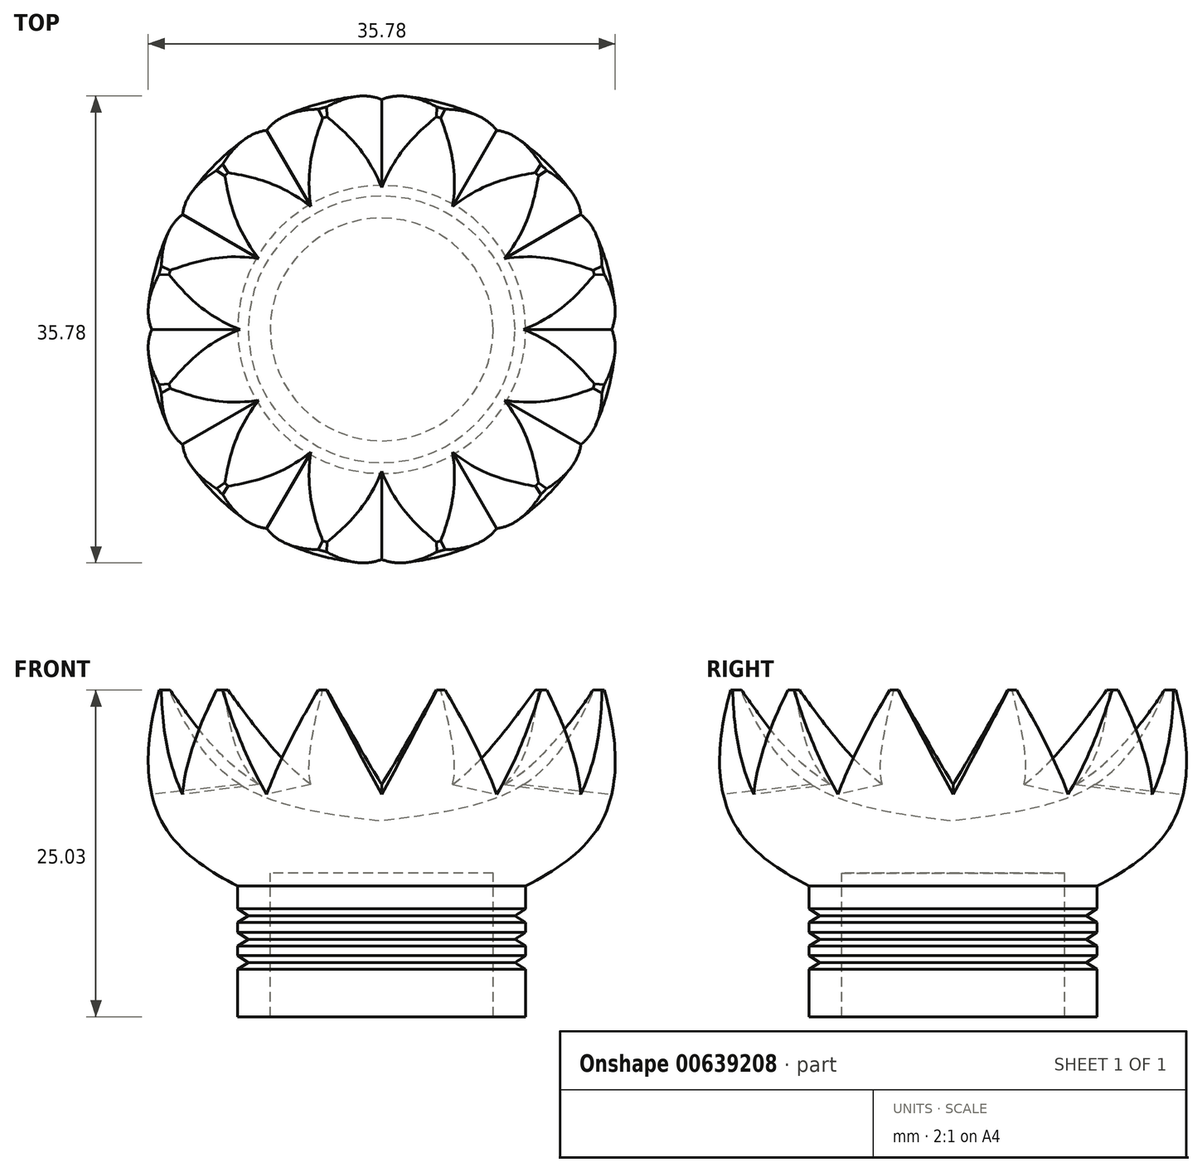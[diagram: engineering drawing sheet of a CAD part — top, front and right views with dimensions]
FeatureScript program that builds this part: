
annotation { "Feature Type Name" : "Feature", "Feature Type Description" : "" }
export const myFeature = defineFeature(function(context is Context, id is Id, definition is map)
    precondition{}
    {
        {
            var Q0;
            Q0=qCreatedBy(makeId("Front.planeOp"),FACE);
            var sketch = newSketch(context, id + "F0", { "sketchPlane" : qUnion([Q0])});
            skLineSegment(sketch, "E0", {"start": v(0, 11) * mm, "end": v(-8.54, 11) * mm});
            skLineSegment(sketch, "E1", {"start": v(-8.54, 11) * mm, "end": v(-8.54, 0) * mm});
            skLineSegment(sketch, "E2", {"start": v(-8.54, 0) * mm, "end": v(-11.04, 0) * mm});
            skLineSegment(sketch, "E3", {"start": v(-11.04, 0) * mm, "end": v(-11.04, 3.63) * mm});
            skLineSegment(sketch, "E4", {"start": v(-11.04, 3.63) * mm, "end": v(-10.22, 4.14) * mm});
            skLineSegment(sketch, "E5", {"start": v(-10.22, 4.14) * mm, "end": v(-11.04, 4.68) * mm});
            skLineSegment(sketch, "E6", {"start": v(-11.04, 4.68) * mm, "end": v(-11.04, 5.42) * mm});
            skLineSegment(sketch, "E7", {"start": v(-11.04, 5.42) * mm, "end": v(-10.22, 5.94) * mm});
            skLineSegment(sketch, "E8", {"start": v(-10.22, 5.94) * mm, "end": v(-11.04, 6.47) * mm});
            skLineSegment(sketch, "E9", {"start": v(-11.04, 6.47) * mm, "end": v(-11.04, 7.21) * mm});
            skLineSegment(sketch, "E10", {"start": v(-11.04, 7.21) * mm, "end": v(-10.22, 7.73) * mm});
            skLineSegment(sketch, "E11", {"start": v(-10.22, 7.73) * mm, "end": v(-11.04, 8.27) * mm});
            skLineSegment(sketch, "E12", {"start": v(-11.04, 8.27) * mm, "end": v(-11.04, 9) * mm});
            skLineSegment(sketch, "E13", {"start": v(-11.04, 9) * mm, "end": v(-11.04, 10.01) * mm});
            skFitSpline(sketch, "E14", {"points": [v(-11.04, 10.01) * mm, v(-16.97, 15.17) * mm, v(-17.56, 25.03) * mm], "startDerivative": vector(-16.56, 8.68) * mm, "endDerivative": vector(3.17, 21.15) * mm});
            skLineSegment(sketch, "E15", {"start": v(-17.56, 25.03) * mm, "end": v(-16.82, 25.03) * mm});
            skFitSpline(sketch, "E16", {"points": [v(-16.82, 25.03) * mm, v(-10.92, 17.83) * mm, v(0, 15.01) * mm], "startDerivative": vector(10.38, -17.46) * mm, "endDerivative": vector(23.06, -2.82) * mm});
            skLineSegment(sketch, "E17", {"start": v(0, 15.01) * mm, "end": v(0, 11) * mm});
            skSolve(sketch);
        }
        {
            var Q0;
            Q0 = qSketchRegion(id + "F0", true);
            var Q1;
            Q1=sQuery(id+"F0.wireOp",EDGE,"E17");
            revolve(context, id + "F1", {"entities" : qUnion([Q0]), "axis" : qUnion([Q1]), "revolveType" : RevolveType.FULL});
        }
        {
            var Q0;
            Q0=qCreatedBy(makeId("Front.planeOp"),FACE);
            var sketch = newSketch(context, id + "F2", { "sketchPlane" : qUnion([Q0])});
            skLineSegment(sketch, "E18", {"start": v(0, 26.5) * mm, "end": v(4, 26.5) * mm});
            skLineSegment(sketch, "E19", {"start": v(4, 26.5) * mm, "end": v(0, 19) * mm});
            skLineSegment(sketch, "E20.MirrorCS", {"start": v(0, 26.5) * mm, "end": v(-4, 26.5) * mm});
            skLineSegment(sketch, "E21.MirrorCS", {"start": v(-4, 26.5) * mm, "end": v(0, 19) * mm});
            skSolve(sketch);
        }
        {
            var Q0;
            Q0 = qSketchRegion(id + "F2", true);
            extrude(context, id + "F3", {"entities" : qUnion([Q0]), "endBound" : BoundingType.THROUGH_ALL, "depth" : 25 * mm, "offsetDistance" : 25 * mm, "hasDraft" : true, "draftAngle" : 3 * degree});
        }
        {
            var Q0;
            Q0=makeQuery(id+"F3.opExtrude","SWEPT_BODY",BODY,{"disambiguationData":[OSD([sQuery(id+"F2.wireOp",EDGE,"E18"),sQuery(id+"F2.wireOp",EDGE,"E19"),sQuery(id+"F2.wireOp",EDGE,"E20.MirrorCS"),sQuery(id+"F2.wireOp",EDGE,"E21.MirrorCS")])]});
            var Q1;
            Q1=makeQuery(id+"F1.opRevolve","SWEPT_FACE",FACE,{"disambiguationData":[OSD([sQuery(id+"F0.wireOp",EDGE,"E12"),sQuery(id+"F0.wireOp",EDGE,"E13")])]});
            circularPattern(context, id + "F4", {"operationType" : NewBodyOperationType.REMOVE, "entities" : qUnion([Q0]), "axis" : qUnion([Q1]), "angle" : 360 * degree, "instanceCount" : 12, "equalSpace" : true});
        }
    });
